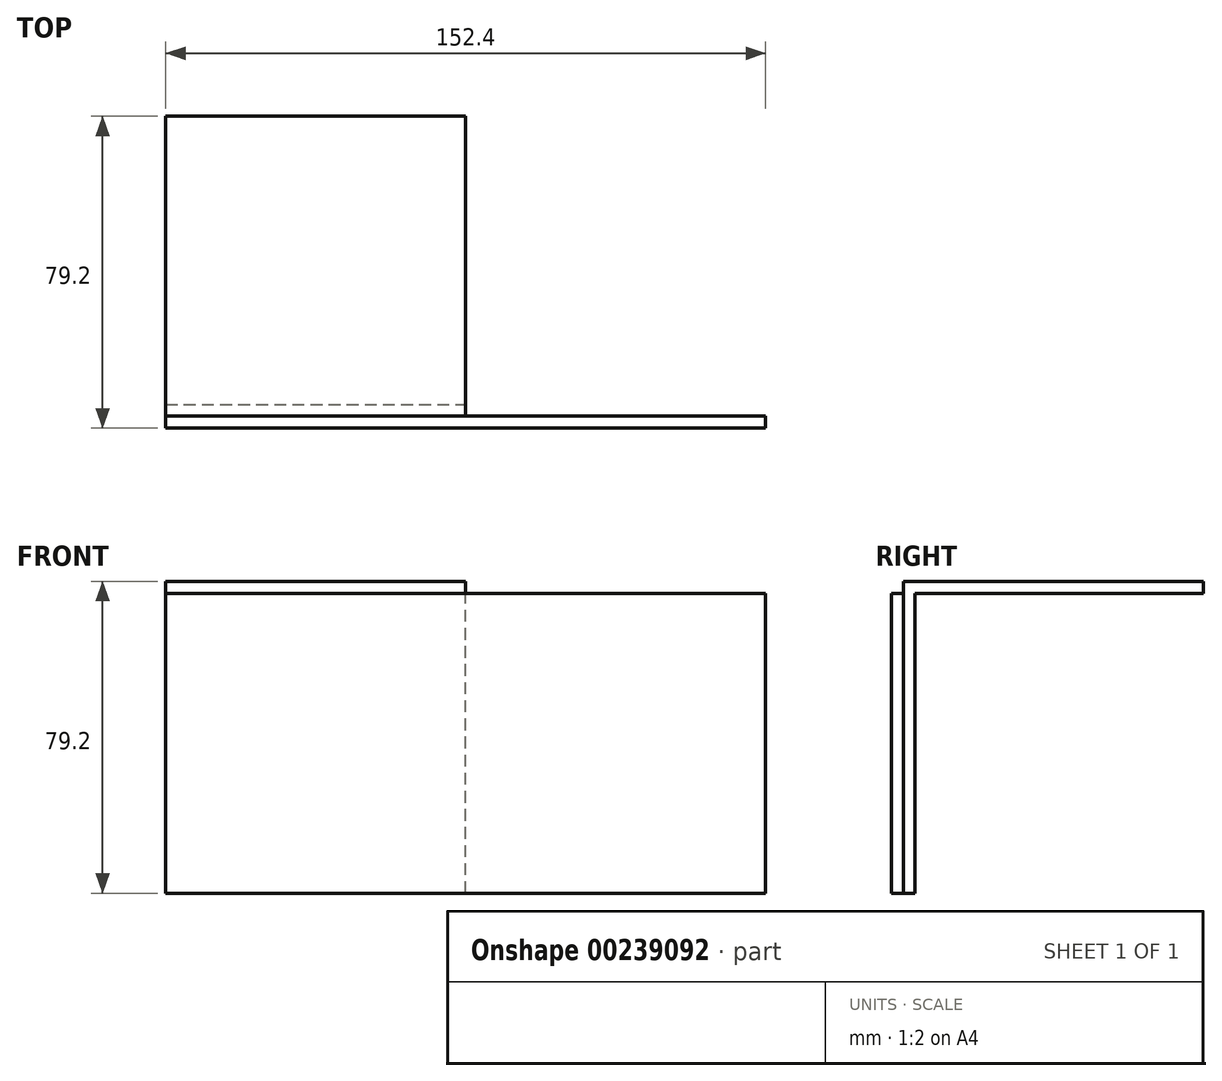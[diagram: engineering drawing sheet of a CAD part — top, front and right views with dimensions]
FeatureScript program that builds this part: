
annotation { "Feature Type Name" : "Feature", "Feature Type Description" : "" }
export const myFeature = defineFeature(function(context is Context, id is Id, definition is map)
    precondition{}
    {
        {
            assignVariable(context, id + "F0", {"name" : "v", "anyValue" : 3});
        }
        {
            var Q0;
            Q0=qCreatedBy(makeId("Front.planeOp"),FACE);
            var sketch = newSketch(context, id + "F1", { "sketchPlane" : qUnion([Q0])});
            skLineSegment(sketch, "E0.bottom", {"start": v(-76.2, 33.04) * mm, "end": v(76.2, 33.04) * mm});
            skLineSegment(sketch, "E0.top", {"start": v(-76.2, -43.16) * mm, "end": v(76.2, -43.16) * mm});
            skLineSegment(sketch, "E0.left", {"start": v(-76.2, 33.04) * mm, "end": v(-76.2, -43.16) * mm});
            skLineSegment(sketch, "E0.right", {"start": v(76.2, 33.04) * mm, "end": v(76.2, -43.16) * mm});
            skPoint(sketch, "E0.middle", {"position": v(0, -5.06) * mm});
            skSolve(sketch);
        }
        {
            var Q0;
            Q0 = qSketchRegion(id + "F1", true);
            extrude(context, id + "F2", {"entities" : qUnion([Q0]), "depth" : (getVariable(context, 'v')) * mm});
        }
        {
            var Q0;
            Q0=makeQuery(id+"F2.opExtrude","CAP_FACE",FACE,{"disambiguationData":[OSD([sQuery(id+"F1.wireOp",EDGE,"E0.bottom"),sQuery(id+"F1.wireOp",EDGE,"E0.top"),sQuery(id+"F1.wireOp",EDGE,"E0.left"),sQuery(id+"F1.wireOp",EDGE,"E0.right")])],"isStart":true});
            var sketch = newSketch(context, id + "F3", { "sketchPlane" : qUnion([Q0])});
            skLineSegment(sketch, "E1.bottom", {"start": v(76.2, -43.16) * mm, "end": v(0, -43.16) * mm});
            skLineSegment(sketch, "E1.top", {"start": v(76.2, 33.04) * mm, "end": v(0, 33.04) * mm});
            skLineSegment(sketch, "E1.left", {"start": v(76.2, -43.16) * mm, "end": v(76.2, 33.04) * mm});
            skLineSegment(sketch, "E1.right", {"start": v(0, -43.16) * mm, "end": v(0, 33.04) * mm});
            skSolve(sketch);
        }
        {
            var Q0;
            Q0 = qSketchRegion(id + "F3", true);
            extrude(context, id + "F4", {"entities" : qUnion([Q0]), "operationType" : NewBodyOperationType.ADD, "depth" : (getVariable(context, 'v')) * mm});
        }
        {
            var Q0;
            Q0=makeQuery(id+"F4.boolean.opBoolean","MERGE",FACE,{"derivedFrom":[makeQuery(id+"F2.opExtrude","SWEPT_FACE",FACE,{"disambiguationData":[OSD([sQuery(id+"F1.wireOp",EDGE,"E0.bottom")])]}),makeQuery(id+"F4.opExtrude","SWEPT_FACE",FACE,{"disambiguationData":[OSD([sQuery(id+"F3.wireOp",EDGE,"E1.top")])]})]});
            var sketch = newSketch(context, id + "F5", { "sketchPlane" : qUnion([Q0])});
            skLineSegment(sketch, "E2.bottom", {"start": v(-76.2, 76.2) * mm, "end": v(0, 76.2) * mm});
            skLineSegment(sketch, "E2.top", {"start": v(-76.2, 0) * mm, "end": v(0, 0) * mm});
            skLineSegment(sketch, "E2.left", {"start": v(-76.2, 76.2) * mm, "end": v(-76.2, 0) * mm});
            skLineSegment(sketch, "E2.right", {"start": v(0, 76.2) * mm, "end": v(0, 0) * mm});
            skSolve(sketch);
        }
        {
            var Q0;
            Q0 = qSketchRegion(id + "F5", true);
            extrude(context, id + "F6", {"entities" : qUnion([Q0]), "operationType" : NewBodyOperationType.ADD, "depth" : (getVariable(context, 'v')) * mm});
        }
    });
